# Revit family: ШУВ-Ч-С300
name_source: partatom
category: Оборудование
units: mm (PartAtom-declared; Revit-internal decimal feet)

## family parameters
Всегда вертикально = Да
Классификация = Нет
На основе рабочей плоскости = Нет
Общий = Нет
При загрузке вырезать с полостями = Нет
Размер круглого соединителя = Использовать диаметр
Тип детали = Нормальный
Точка расчета площади = Нет

## types (2) — shared parameters
URL = https://plazma-t.ru
Группа модели = ШУВ-Ч-С300
Изготовитель = ООО "Плазма-Т"
Назв гориз ПУШ = 120 мм
Описание = ШУВ-С300 предназначен для управления одно/трехфазным электродвигателем приточного или вытяжного вентилятора системы противопожарной вентиляции от 0,37 до 200 кВт. Управление осуществляется посредством интегрированного модуля контроля и управления МС322-24, что позволяет использовать шкаф в составе Системы пожарной автоматики и сигнализации «СПРУТ-2», в частности – в составе адресно-аналоговой сигнализации «С300».
Расст ввод от задней стенки = 100 мм
Расст вывода от задней стенки = 125 мм
Расст вывода от левой стенки = 100 мм
Расст вывода2 от левой стенки = 160 мм
Расст вывода3 от левой стенки = 220 мм
zero-valued in all types: Отметка по умолчанию

## per-type parameters (varying)
| type | Комментарии к типоразмеру | Расст ПУШ от верхней стенки | Расст ПУШ от левой стенки | Расст ввод от левой стенки | Расст замок | расст замок верт |
| ШУВ-М_АВВ_0,37-7,5кВт | Ш3/ABB | 100 мм | 110 мм | 350 мм | 450 мм | 350 мм |
| ШУВ-М_АВВ_11-18,5кВт | Ш4/ABB | 110 мм | 220 мм | 160 мм | 550 мм | 400 мм |
